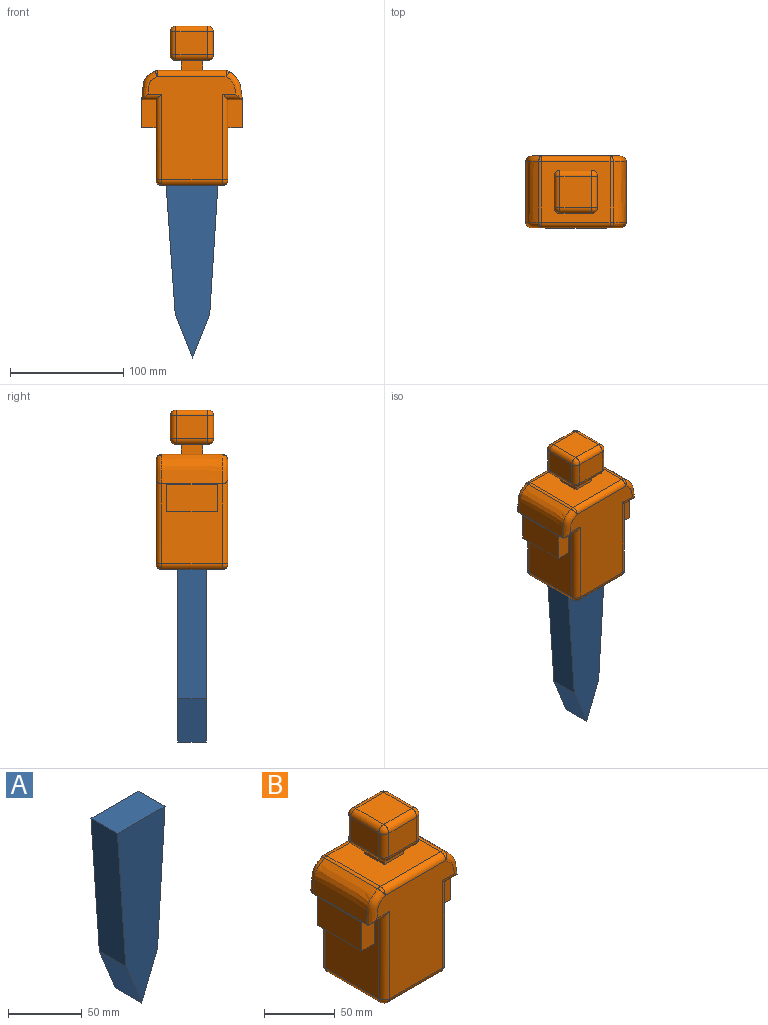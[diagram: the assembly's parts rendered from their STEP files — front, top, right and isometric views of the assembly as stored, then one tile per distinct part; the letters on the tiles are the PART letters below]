
ASSEMBLY  parts=2 mates=1
PART A: 7 faces, bbox 45.7x25.4x152.4 mm
  f0: plane 45.72x25.4mm, normal (0,0,1), area 1161.3mm2, adj f1,f4,f5,f6
  f1: plane 114.3x25.4mm, normal (-1,0,-0.07), area 2910.4mm2, adj f0,f2,f5,f6
  f2: plane 38.1x25.4mm, normal (-0.93,0,-0.37), area 1042.3mm2, adj f1,f3,f5,f6
  f3: plane 38.1x25.4mm, normal (0.93,0,-0.37), area 1042.3mm2, adj f2,f4,f5,f6
  f4: plane 114.3x25.4mm, normal (1,0,-0.06), area 2909mm2, adj f0,f3,f5,f6
  f5: plane 152.4x45.72mm, normal (0,-1,0), area 4935.5mm2, adj f0,f1,f2,f3,f4
  f6: plane 152.4x45.72mm, normal (0,1,0), area 4935.5mm2, adj f0,f1,f2,f3,f4
PART B: 80 faces, bbox 89.6x63.5x140.9 mm
  f0: plane 12.69x4.45mm, normal (0,0,-1), area 56.4mm2, adj f1,f29,f32,f33
  f1: plane 70.63x53.34mm, normal (-1,0,0), area 2660.2mm2, adj f0,f20,f27,f28,f29,f30,f34,f35
  f2: plane 12.69x4.45mm, normal (0,0,-1), area 56.4mm2, adj f3,f25,f58,f59
  f3: plane 70.63x53.34mm, normal (1,0,0), area 2660.2mm2, adj f2,f18,f22,f24,f25,f45,f51,f54
  f4: plane 19.05x8.79mm, normal (-1,0,0), area 167.5mm2, adj f6,f7,f8,f14
  f5: plane 19.05x8.79mm, normal (1,0,0), area 167.5mm2, adj f6,f7,f8,f14
  f6: plane 19.05x8.79mm, normal (0,-1,0), area 167.5mm2, adj f4,f5,f8,f14
  f7: plane 19.05x8.79mm, normal (0,1,0), area 167.5mm2, adj f4,f5,f8,f14
  f8: plane 27.94x27.94mm, normal (0,0,-1), area 417.7mm2, adj f4,f5,f6,f7,f60,f61,f62,f63
  f9: plane 27.94x20.32mm, normal (1,0,0), area 567.7mm2, adj f63,f67,f75,f78
  f10: plane 27.94x27.94mm, normal (0,0,1), area 780.6mm2, adj f64,f65,f66,f67
  f11: plane 27.94x20.32mm, normal (-1,0,0), area 567.7mm2, adj f60,f64,f69,f72
  f12: plane 27.94x20.32mm, normal (0,-1,0), area 567.7mm2, adj f61,f65,f69,f75
  f13: plane 27.94x20.32mm, normal (0,1,0), area 567.7mm2, adj f62,f66,f72,f78
  f14: plane 60.45x53.34mm, normal (0,0,1), area 2861.5mm2, adj f4,f5,f6,f7,f38,f47,f48,f49
  f15: plane 53.34x53.34mm, normal (0,0,-1), area 2845.2mm2, adj f35,f41,f44,f45
  f16: plane 91.44x77.51mm, normal (0,-1,0), area 5187.4mm2, adj f30,f31,f37,f41,f47,f51,f55,f56
  f17: plane 91.44x77.51mm, normal (0,1,0), area 5187.4mm2, adj f33,f34,f39,f44,f49,f54,f57,f58
  f18: plane 12.69x4.45mm, normal (0,0,-1), area 56.4mm2, adj f3,f24,f55,f59
  f19: extruded ~53.34x24.49mm, area 1504.1mm2, adj f48,f56,f57,f59
  f20: plane 12.69x4.45mm, normal (0,0,-1), area 56.4mm2, adj f1,f28,f31,f32
  f21: extruded ~53.34x24.91mm, area 1566.6mm2, adj f32,f37,f38,f39
  f22: plane 44.45x12.7mm, normal (0,0,-1), area 564.5mm2, adj f3,f23,f24,f25
  f23: plane 44.45x24.58mm, normal (1,0,0), area 1092.4mm2, adj f22,f24,f25,f59
  f24: plane 24.91x12.7mm, normal (0,-1,0), area 316.4mm2, adj f3,f18,f22,f23,f59
  f25: plane 24.91x12.7mm, normal (0,1,0), area 316.4mm2, adj f2,f3,f22,f23,f59
  f26: plane 44.45x24.61mm, normal (-1,0,0), area 1093.8mm2, adj f27,f28,f29,f32
  f27: plane 44.45x12.7mm, normal (0,0,-1), area 564.5mm2, adj f1,f26,f28,f29
  f28: plane 24.91x12.7mm, normal (0,-1,0), area 316.4mm2, adj f1,f20,f26,f27,f32
  f29: plane 24.91x12.7mm, normal (0,1,0), area 316.4mm2, adj f0,f1,f26,f27,f32
  f30: cylinder r=5.08mm len=75.71mm, axis (0,0,1), area 583.9mm2, adj f1,f16,f31,f36
  f31: cylinder r=5.08mm len=17.77mm, axis (-1,0,0), area 99.6mm2, adj f16,f20,f30,f32,f37
  f32: cylinder r=5.08mm len=53.93mm, axis (0,1,0), area 29.5mm2, adj f0,f20,f21,f26,f28,f29,f31,f33
  f33: cylinder r=5.08mm len=17.77mm, axis (1,0,0), area 99.6mm2, adj f0,f17,f32,f34,f39
  f34: cylinder r=5.08mm len=75.71mm, axis (0,0,-1), area 583.9mm2, adj f1,f17,f33,f40
  f35: cylinder r=5.08mm len=53.34mm, axis (0,1,0), area 425.6mm2, adj f1,f15,f36,f40
  f36: sphere r=5.08mm, area 40.5mm2, adj f30,f35,f41
  f37: bspline ~26.79x14.85mm, area 206.4mm2, adj f16,f21,f31,f32,f42
  f38: cylinder r=5.08mm len=53.34mm, axis (0,1,0), area 141.5mm2, adj f14,f21,f42,f43
  f39: bspline ~26.79x14.85mm, area 206.4mm2, adj f17,f21,f32,f33,f43
  f40: sphere r=5.08mm, area 55.3mm2, adj f34,f35,f44
  f41: cylinder r=5.08mm len=53.34mm, axis (-1,0,0), area 425.6mm2, adj f15,f16,f36,f46
  f42: sphere r=5.08mm, area 13.5mm2, adj f37,f38,f47
  f43: sphere r=5.08mm, area 13.5mm2, adj f38,f39,f49
  f44: cylinder r=5.08mm len=53.34mm, axis (1,0,0), area 425.6mm2, adj f15,f17,f40,f50
  f45: cylinder r=5.08mm len=53.34mm, axis (0,-1,0), area 425.6mm2, adj f3,f15,f46,f50
  f46: sphere r=5.08mm, area 40.5mm2, adj f41,f45,f51
  f47: cylinder r=5.08mm len=60.45mm, axis (1,0,0), area 482.4mm2, adj f14,f16,f42,f52
  f48: cylinder r=5.08mm len=53.34mm, axis (0,1,0), area 178.8mm2, adj f14,f19,f52,f53
  f49: cylinder r=5.08mm len=60.45mm, axis (-1,0,0), area 482.4mm2, adj f14,f17,f43,f53
  f50: sphere r=5.08mm, area 25.8mm2, adj f44,f45,f54
  f51: cylinder r=5.08mm len=75.71mm, axis (0,0,-1), area 583.9mm2, adj f3,f16,f46,f55
  f52: sphere r=5.08mm, area 17mm2, adj f47,f48,f56
  f53: sphere r=5.08mm, area 23.3mm2, adj f48,f49,f57
  f54: cylinder r=5.08mm len=75.71mm, axis (0,0,1), area 583.9mm2, adj f3,f17,f50,f58
  f55: cylinder r=5.08mm len=17.77mm, axis (-1,0,0), area 99.3mm2, adj f16,f18,f51,f56,f59
  f56: bspline ~31.26x16.23mm, area 199.3mm2, adj f16,f19,f52,f55,f59
  f57: bspline ~31.41x16.42mm, area 199.3mm2, adj f17,f19,f53,f58,f59
  f58: cylinder r=5.08mm len=17.77mm, axis (1,0,0), area 99.3mm2, adj f2,f17,f54,f57,f59
  f59: cylinder r=5.08mm len=53.99mm, axis (0,1,0), area 32.7mm2, adj f2,f18,f19,f23,f24,f25,f55,f56
  f60: cylinder r=5.08mm len=27.94mm, axis (0,-1,0), area 223mm2, adj f8,f11,f70,f73
  f61: cylinder r=5.08mm len=27.94mm, axis (-1,0,0), area 223mm2, adj f8,f12,f70,f76
  f62: cylinder r=5.08mm len=27.94mm, axis (1,0,0), area 223mm2, adj f8,f13,f73,f79
  f63: cylinder r=5.08mm len=27.94mm, axis (0,1,0), area 223mm2, adj f8,f9,f76,f79
  f64: cylinder r=5.08mm len=27.94mm, axis (0,1,0), area 223mm2, adj f10,f11,f68,f71
  f65: cylinder r=5.08mm len=27.94mm, axis (1,0,0), area 223mm2, adj f10,f12,f68,f74
  f66: cylinder r=5.08mm len=27.94mm, axis (-1,0,0), area 223mm2, adj f10,f13,f71,f77
  f67: cylinder r=5.08mm len=27.94mm, axis (0,-1,0), area 223mm2, adj f9,f10,f74,f77
  f68: sphere r=5.08mm, area 40.5mm2, adj f64,f65,f69
  f69: cylinder r=5.08mm len=20.32mm, axis (0,0,1), area 162.1mm2, adj f11,f12,f68,f70
  f70: sphere r=5.08mm, area 40.5mm2, adj f60,f61,f69
  f71: sphere r=5.08mm, area 40.5mm2, adj f64,f66,f72
  f72: cylinder r=5.08mm len=20.32mm, axis (0,0,-1), area 162.1mm2, adj f11,f13,f71,f73
  f73: sphere r=5.08mm, area 55.3mm2, adj f60,f62,f72
  f74: sphere r=5.08mm, area 40.5mm2, adj f65,f67,f75
  f75: cylinder r=5.08mm len=20.32mm, axis (0,0,-1), area 162.1mm2, adj f9,f12,f74,f76
  f76: sphere r=5.08mm, area 40.5mm2, adj f61,f63,f75
  f77: sphere r=5.08mm, area 25.8mm2, adj f66,f67,f78
  f78: cylinder r=5.08mm len=20.32mm, axis (0,0,1), area 162.1mm2, adj f9,f13,f77,f79
  f79: sphere r=5.08mm, area 40.5mm2, adj f62,f63,f78
PLACE A t=(207.69,-75.64,-351.04)mm
PLACE B t=(207.28,-88.34,-195.17)mm
MATE fastened A.f0 <-> B.f15  axis (0,0,1) through (207.28,-88.34,-245.97)mm
